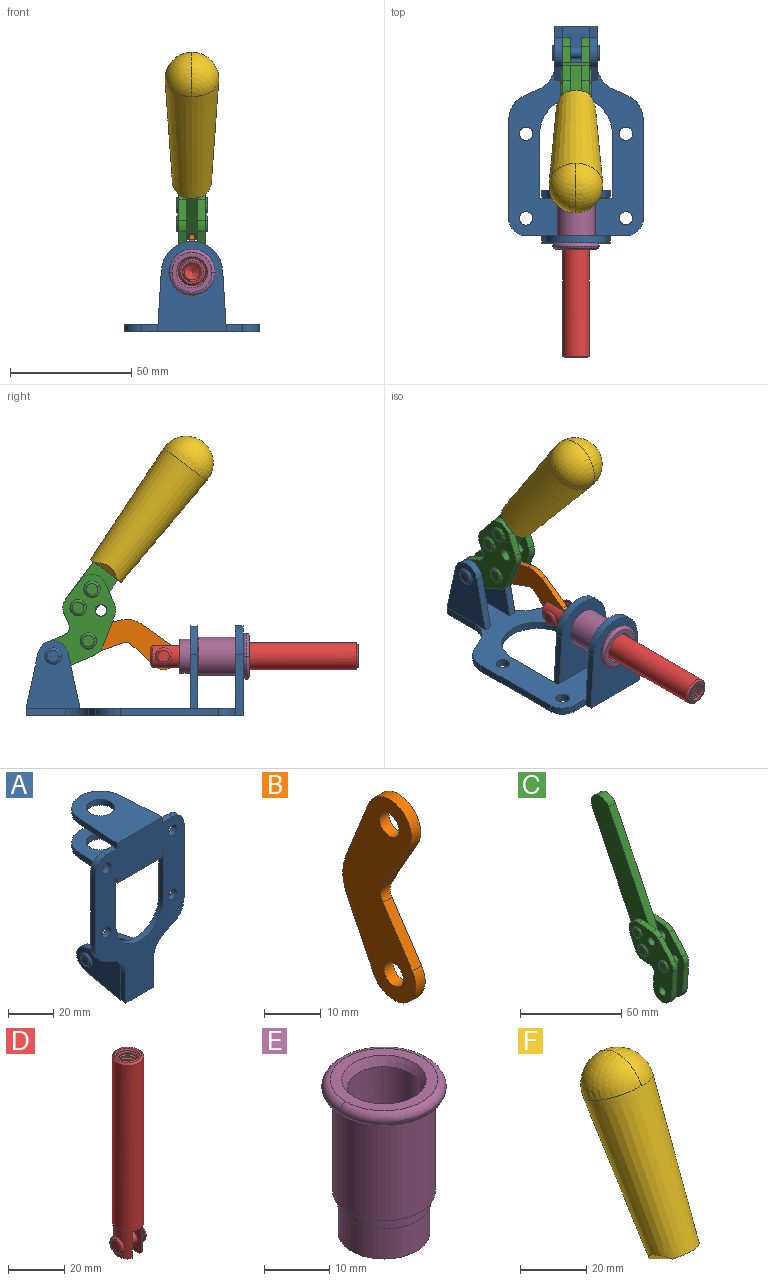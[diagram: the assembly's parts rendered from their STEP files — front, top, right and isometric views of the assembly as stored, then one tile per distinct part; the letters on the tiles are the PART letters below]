
ASSEMBLY  parts=6 mates=6
PART A: 55 faces, bbox 55.7x37.4x89.8 mm
  f0: torus R=2.41mm, axis (-1,0,0), area 15mm2, adj f11,f15,f25
  f1: torus R=2.41mm, axis (-1,0,0), area 15mm2, adj f10,f12,f22
  f2: cylinder r=2.78mm len=5.56mm, axis (0,-1,0), area 54.2mm2, adj f30,f54
  f3: cylinder r=14.99mm len=29.97mm, axis (0,-1,0), area 145.9mm2, adj f30,f49,f53,f54
  f4: cylinder r=2.78mm len=5.56mm, axis (0,-1,0), area 54.2mm2, adj f30,f54
  f5: cylinder r=2.78mm len=5.56mm, axis (0,-1,0), area 54.2mm2, adj f30,f54
  f6: cylinder r=2.78mm len=5.56mm, axis (0,-1,0), area 54.2mm2, adj f30,f54
  f7: cylinder r=6.35mm len=12.7mm, axis (0,0,1), area 123.6mm2, adj f27,f51
  f8: cylinder r=6.35mm len=12.7mm, axis (0,0,-1), area 124.7mm2, adj f21,f35
  f9: cylinder r=2.41mm len=11.18mm, axis (-1,0,0), area 169.4mm2, adj f16,f19
  f10: plane 4.83x4.83mm, normal (1,0,0), area 18.3mm2, adj f1,f12
  f11: plane 4.83x4.83mm, normal (-1,0,0), area 18.3mm2, adj f0,f15
  f12: torus R=2.41mm, axis (-1,0,0), area 15mm2, adj f1,f10,f22
  f13: cylinder r=6.35mm len=12.41mm, axis (1,0,0), area 53.4mm2, adj f18,f19,f22,f23
  f14: cylinder r=6.35mm len=12.41mm, axis (-1,0,0), area 53.4mm2, adj f16,f17,f24,f25
  f15: torus R=2.41mm, axis (-1,0,0), area 15mm2, adj f0,f11,f25
  f16: plane 27.86x22.35mm, normal (1,0,0), area 425.4mm2, adj f9,f14,f17,f24,f30
  f17: plane 22.86x4.97mm, normal (0,0.21,0.98), area 72.5mm2, adj f14,f16,f25,f30
  f18: plane 22.86x4.97mm, normal (0,0.21,0.98), area 72.5mm2, adj f13,f19,f22,f30
  f19: plane 27.86x22.35mm, normal (-1,0,0), area 425.4mm2, adj f9,f13,f18,f23,f30
  f20: cylinder r=12.7mm len=25.35mm, axis (0,0,-1), area 119.8mm2, adj f21,f34,f35,f36
  f21: plane 34.21x28.07mm, normal (0,0,-1), area 702.4mm2, adj f8,f20,f30,f34,f36
  f22: plane 27.96x22.45mm, normal (1,0,0), area 407.2mm2, adj f1,f12,f13,f18,f23,f30,f42,f43
  f23: plane 22.86x4.97mm, normal (0,0.21,-0.98), area 72.5mm2, adj f13,f19,f22,f44
  f24: plane 22.86x4.97mm, normal (0,0.21,-0.98), area 72.5mm2, adj f14,f16,f25,f44
  f25: plane 27.86x22.35mm, normal (-1,0,0), area 407.1mm2, adj f0,f14,f15,f17,f24,f30,f45,f46
  f26: plane 3.1x0.95mm, normal (0,0,-1), area 2.7mm2, adj f30,f49,f50,f54
  f27: plane 34.21x28.07mm, normal (0,0,1), area 702.4mm2, adj f7,f28,f30,f50,f52
  f28: cylinder r=12.7mm len=25.35mm, axis (0,0,1), area 118.8mm2, adj f27,f50,f51,f52
  f29: plane 3.1x0.95mm, normal (0,0,-1), area 2.7mm2, adj f30,f52,f53,f54
  f30: plane 86.54x55.63mm, normal (0,1,0), area 2362.9mm2, adj f2,f3,f4,f5,f6,f16,f17,f18
  f31: plane 40.56x3.1mm, normal (-1,0,0), area 125.7mm2, adj f30,f32,f48,f54
  f32: cylinder r=7.11mm len=7.11mm, axis (0,-1,0), area 34.6mm2, adj f30,f31,f33,f54
  f33: plane 6.67x3.1mm, normal (0,0,1), area 20.4mm2, adj f30,f32,f34,f54
  f34: plane 25.39x3.13mm, normal (-1,0.06,0), area 79.5mm2, adj f20,f21,f33,f35,f54
  f35: plane 37.31x28.45mm, normal (0,0,1), area 789.9mm2, adj f8,f20,f34,f36,f54
  f36: plane 25.39x3.13mm, normal (1,0.06,0), area 79.5mm2, adj f20,f21,f35,f37,f54
  f37: plane 6.67x3.1mm, normal (0,0,1), area 20.4mm2, adj f30,f36,f38,f54
  f38: cylinder r=7.11mm len=7.11mm, axis (0,-1,0), area 34.6mm2, adj f30,f37,f39,f54
  f39: plane 40.56x3.1mm, normal (1,0,0), area 125.7mm2, adj f30,f38,f40,f54
  f40: cylinder r=11.18mm len=10.16mm, axis (0,-1,0), area 39.5mm2, adj f30,f39,f41,f54
  f41: plane 6.09x3.1mm, normal (0.42,0,-0.91), area 20.8mm2, adj f30,f40,f42,f54
  f42: cylinder r=11.18mm len=9.41mm, axis (0,-1,0), area 37.2mm2, adj f22,f30,f41,f43,f54
  f43: plane 16.5x3.1mm, normal (1,0,0), area 51.1mm2, adj f22,f42,f44,f54
  f44: plane 17.37x3.1mm, normal (0,0,-1), area 53.8mm2, adj f23,f24,f30,f43,f45,f54
  f45: plane 16.5x3.1mm, normal (-1,0,0), area 51.1mm2, adj f25,f44,f46,f54
  f46: cylinder r=11.18mm len=9.41mm, axis (0,-1,0), area 37.2mm2, adj f25,f30,f45,f47,f54
  f47: plane 6.09x3.1mm, normal (-0.42,0,-0.91), area 20.8mm2, adj f30,f46,f48,f54
  f48: cylinder r=11.18mm len=10.16mm, axis (0,-1,0), area 39.5mm2, adj f30,f31,f47,f54
  f49: plane 26.54x3.1mm, normal (-1,0,0), area 82.3mm2, adj f3,f26,f30,f54
  f50: plane 25.39x3.1mm, normal (1,0.06,0), area 78.8mm2, adj f26,f27,f28,f51,f54
  f51: plane 37.31x28.45mm, normal (0,0,-1), area 789.9mm2, adj f7,f28,f50,f52,f54
  f52: plane 25.39x3.1mm, normal (-1,0.06,0), area 78.8mm2, adj f27,f28,f29,f51,f54
  f53: plane 26.54x3.1mm, normal (1,0,0), area 82.3mm2, adj f3,f29,f30,f54
  f54: plane 89.66x55.63mm, normal (0,-1,0), area 2678.5mm2, adj f2,f3,f4,f5,f6,f26,f29,f31
PART B: 12 faces, bbox 2.3x18.2x42.8 mm
  f0: cylinder r=2.4mm len=4.8mm, axis (1,0,0), area 34.9mm2, adj f4,f11
  f1: cylinder r=10.41mm len=8.47mm, axis (1,0,0), area 20.2mm2, adj f4,f9,f10,f11
  f2: cylinder r=3.05mm len=3.16mm, axis (1,0,0), area 7.7mm2, adj f4,f6,f7,f11
  f3: cylinder r=2.4mm len=4.8mm, axis (1,0,0), area 34.9mm2, adj f4,f11
  f4: plane 42.81x18.23mm, normal (-1,0,0), area 414.1mm2, adj f0,f1,f2,f3,f5,f6,f7,f8
  f5: cylinder r=5.54mm len=10.67mm, axis (1,0,0), area 41.8mm2, adj f4,f6,f10,f11
  f6: plane 11.66x6.53mm, normal (0,-0.87,-0.49), area 30.9mm2, adj f2,f4,f5,f11
  f7: plane 11.17x7.33mm, normal (0,-0.84,0.55), area 30.9mm2, adj f2,f4,f8,f11
  f8: cylinder r=5.54mm len=10.51mm, axis (1,0,0), area 41.8mm2, adj f4,f7,f9,f11
  f9: plane 13.67x6.67mm, normal (0,0.9,-0.44), area 35.1mm2, adj f1,f4,f8,f11
  f10: plane 14.1x5.7mm, normal (0,0.93,0.37), area 35.1mm2, adj f1,f4,f5,f11
  f11: plane 42.81x18.23mm, normal (1,0,0), area 414.1mm2, adj f0,f1,f2,f3,f5,f6,f7,f8
PART C: 59 faces, bbox 12.9x60.2x99.6 mm
  f0: torus R=2.39mm, axis (-1,0,0), area 14.9mm2, adj f20,f43,f51
  f1: torus R=2.39mm, axis (-1,0,0), area 14.9mm2, adj f19,f42,f51
  f2: torus R=2.39mm, axis (-1,0,0), area 14.9mm2, adj f18,f35,f51
  f3: torus R=2.39mm, axis (-1,0,0), area 14.9mm2, adj f14,f17,f23
  f4: torus R=2.39mm, axis (-1,0,0), area 14.9mm2, adj f13,f16,f23
  f5: torus R=2.39mm, axis (-1,0,0), area 14.9mm2, adj f12,f15,f23
  f6: cylinder r=2.39mm len=4.78mm, axis (1,0,0), area 46.5mm2, adj f48,f50,f51
  f7: cylinder r=2.39mm len=4.78mm, axis (1,0,0), area 46.5mm2, adj f50,f51
  f8: cylinder r=6.35mm len=12.68mm, axis (1,0,0), area 61.8mm2, adj f38,f39,f50,f51
  f9: cylinder r=2.39mm len=4.78mm, axis (-1,0,0), area 70.5mm2, adj f46,f50
  f10: cylinder r=2.39mm len=4.78mm, axis (-1,0,0), area 46.5mm2, adj f23,f45,f46
  f11: cylinder r=2.39mm len=4.78mm, axis (-1,0,0), area 46.5mm2, adj f23,f46
  f12: plane 4.78x4.78mm, normal (1,0,0), area 17.9mm2, adj f5,f15
  f13: plane 4.78x4.78mm, normal (1,0,0), area 17.9mm2, adj f4,f16
  f14: plane 4.78x4.78mm, normal (1,0,0), area 17.9mm2, adj f3,f17
  f15: torus R=2.39mm, axis (-1,0,0), area 14.9mm2, adj f5,f12,f23
  f16: torus R=2.39mm, axis (-1,0,0), area 14.9mm2, adj f4,f13,f23
  f17: torus R=2.39mm, axis (-1,0,0), area 14.9mm2, adj f3,f14,f23
  f18: plane 4.78x4.78mm, normal (-1,0,0), area 17.9mm2, adj f2,f35
  f19: plane 4.78x4.78mm, normal (-1,0,0), area 17.9mm2, adj f1,f42
  f20: plane 4.78x4.78mm, normal (-1,0,0), area 17.9mm2, adj f0,f43
  f21: plane 2.26x0.2mm, normal (1,0,0), area 0.2mm2, adj f31,f44
  f22: plane 2.26x0.2mm, normal (-1,0,0), area 0.2mm2, adj f41,f44
  f23: plane 39.37x30.77mm, normal (1,0,0), area 565.5mm2, adj f3,f4,f5,f10,f11,f15,f16,f17
  f24: cylinder r=6.1mm len=4.15mm, axis (-1,0,0), area 14.7mm2, adj f23,f25,f32,f46
  f25: plane 10.25x9.01mm, normal (0,-0.75,0.66), area 42.3mm2, adj f23,f24,f26,f46
  f26: cylinder r=6.35mm len=4.64mm, axis (-1,0,0), area 15.6mm2, adj f23,f25,f27,f46
  f27: plane 15.84x3.1mm, normal (0,-1,-0.07), area 49.2mm2, adj f23,f26,f28,f46
  f28: cylinder r=6.35mm len=12.68mm, axis (-1,0,0), area 61.8mm2, adj f23,f27,f29,f46
  f29: plane 8.11x3.1mm, normal (0,1,0.07), area 25.2mm2, adj f23,f28,f30,f46
  f30: cylinder r=3.05mm len=3.25mm, axis (-1,0,0), area 14.8mm2, adj f23,f29,f31,f46
  f31: plane 5.99x3.1mm, normal (0,0.07,-1), area 18.6mm2, adj f21,f23,f30,f44,f46
  f32: plane 9.5x3.1mm, normal (0,-0.07,1), area 29.5mm2, adj f23,f24,f33,f46,f47
  f33: cylinder r=6.1mm len=8.63mm, axis (-1,0,0), area 39.1mm2, adj f23,f32,f34,f47
  f34: plane 8.65x3.96mm, normal (0,0.91,-0.42), area 29.5mm2, adj f23,f33,f44,f47
  f35: torus R=2.39mm, axis (-1,0,0), area 14.9mm2, adj f2,f18,f51
  f36: plane 10.25x9.01mm, normal (0,-0.75,0.66), area 42.3mm2, adj f37,f49,f50,f51
  f37: cylinder r=6.35mm len=4.64mm, axis (1,0,0), area 15.6mm2, adj f36,f38,f50,f51
  f38: plane 15.84x3.1mm, normal (0,-1,-0.07), area 49.2mm2, adj f8,f37,f50,f51
  f39: plane 8.11x3.1mm, normal (0,1,0.07), area 25.2mm2, adj f8,f40,f50,f51
  f40: cylinder r=3.05mm len=3.25mm, axis (1,0,0), area 14.8mm2, adj f39,f41,f50,f51
  f41: plane 5.99x3.1mm, normal (0,0.07,-1), area 18.6mm2, adj f22,f40,f44,f50,f51
  f42: torus R=2.39mm, axis (-1,0,0), area 14.9mm2, adj f1,f19,f51
  f43: torus R=2.39mm, axis (-1,0,0), area 14.9mm2, adj f0,f20,f51
  f44: cylinder r=6.35mm len=12.12mm, axis (-1,0,0), area 128.9mm2, adj f21,f22,f23,f31,f34,f41,f46,f47
  f45: plane 2.65x1.35mm, normal (1,0,0), area 1mm2, adj f10,f55
  f46: plane 39.08x20.42mm, normal (-1,0,0), area 412.5mm2, adj f9,f10,f11,f24,f25,f26,f27,f28
  f47: plane 77.62x39.82mm, normal (1,0,0), area 850mm2, adj f32,f33,f34,f44,f53,f54,f55
  f48: plane 2.65x1.35mm, normal (-1,0,0), area 1mm2, adj f6,f55
  f49: cylinder r=6.1mm len=4.15mm, axis (1,0,0), area 14.7mm2, adj f36,f50,f51,f56
  f50: plane 39.08x20.42mm, normal (1,0,0), area 412.5mm2, adj f6,f7,f8,f9,f36,f37,f38,f39
  f51: plane 39.37x30.77mm, normal (-1,0,0), area 565.5mm2, adj f0,f1,f2,f6,f7,f8,f35,f36
  f52: plane 8.65x3.96mm, normal (0,0.91,-0.42), area 29.5mm2, adj f44,f51,f57,f58
  f53: plane 68.49x33.4mm, normal (0,0.9,-0.44), area 358.1mm2, adj f44,f47,f54,f58
  f54: cylinder r=6.35mm len=12.06mm, axis (1,0,0), area 93.7mm2, adj f47,f53,f55,f58
  f55: plane 68.49x33.4mm, normal (0,-0.9,0.44), area 358.1mm2, adj f44,f45,f46,f47,f48,f50,f54,f58
  f56: plane 9.5x3.1mm, normal (0,-0.07,1), area 29.5mm2, adj f49,f50,f51,f57,f58
  f57: cylinder r=6.1mm len=8.63mm, axis (1,0,0), area 39.1mm2, adj f51,f52,f56,f58
  f58: plane 77.62x39.82mm, normal (-1,0,0), area 850mm2, adj f44,f52,f53,f54,f55,f56,f57
PART D: 48 faces, bbox 12.6x11.1x86.1 mm
  f0: torus R=2.41mm, axis (-1,0,0), area 15mm2, adj f30,f32,f34
  f1: torus R=2.41mm, axis (-1,0,0), area 15mm2, adj f29,f31,f33
  f2: cylinder r=5.54mm len=72.39mm, axis (0,0,1), area 2518.5mm2, adj f3,f4,f42,f43
  f3: cone r=5.54mm half-angle=45deg, axis (0,0,1), area 7.6mm2, adj f2,f5,f41
  f4: cone r=5.54mm half-angle=45deg, axis (0,0,-1), area 34.9mm2, adj f2,f39
  f5: cylinder r=5.08mm len=11.48mm, axis (0,0,1), area 108.3mm2, adj f3,f7,f8,f41
  f6: cylinder r=2.41mm len=4.83mm, axis (-1,0,0), area 71.2mm2, adj f40,f41
  f7: cylinder r=2.41mm len=4.83mm, axis (-1,0,0), area 7.6mm2, adj f5,f34
  f8: cone r=5.08mm half-angle=45deg, axis (0,0,1), area 10.6mm2, adj f5,f37,f41
  f9: cone r=3.98mm half-angle=45deg, axis (0,0,1), area 17.6mm2, adj f27,f39,f45,f46,f47
  f10: cylinder r=2.41mm len=4.83mm, axis (-1,0,0), area 7.6mm2, adj f33,f38
  f11: cylinder r=3.2mm len=6.4mm, axis (0,0,1), area 78.4mm2, adj f12,f28,f44,f45,f47
  f12: cylinder r=3.2mm len=6.4mm, axis (0,0,1), area 10.5mm2, adj f11,f13,f45,f47
  f13: cylinder r=3.2mm len=6.4mm, axis (0,0,1), area 10.5mm2, adj f12,f14,f45,f47
  f14: cylinder r=3.2mm len=6.4mm, axis (0,0,1), area 10.5mm2, adj f13,f15,f45,f47
  f15: cylinder r=3.2mm len=6.4mm, axis (0,0,1), area 10.5mm2, adj f14,f16,f45,f47
  f16: cylinder r=3.2mm len=6.4mm, axis (0,0,1), area 10.5mm2, adj f15,f17,f45,f47
  f17: cylinder r=3.2mm len=6.4mm, axis (0,0,1), area 10.5mm2, adj f16,f18,f45,f47
  f18: cylinder r=3.2mm len=6.4mm, axis (0,0,1), area 10.5mm2, adj f17,f19,f45,f47
  f19: cylinder r=3.2mm len=6.4mm, axis (0,0,1), area 10.5mm2, adj f18,f20,f45,f47
  f20: cylinder r=3.2mm len=6.4mm, axis (0,0,1), area 10.5mm2, adj f19,f21,f45,f47
  f21: cylinder r=3.2mm len=6.4mm, axis (0,0,1), area 10.5mm2, adj f20,f22,f45,f47
  f22: cylinder r=3.2mm len=6.4mm, axis (0,0,1), area 10.5mm2, adj f21,f23,f45,f47
  f23: cylinder r=3.2mm len=6.4mm, axis (0,0,1), area 10.5mm2, adj f22,f24,f45,f47
  f24: cylinder r=3.2mm len=6.4mm, axis (0,0,1), area 10.5mm2, adj f23,f25,f45,f47
  f25: cylinder r=3.2mm len=6.4mm, axis (0,0,1), area 10.5mm2, adj f24,f26,f45,f47
  f26: cylinder r=3.2mm len=6.4mm, axis (0,0,1), area 10.5mm2, adj f25,f27,f45,f47
  f27: cylinder r=3.2mm len=6.4mm, axis (0,0,1), area 7.4mm2, adj f9,f26,f45,f47
  f28: cone r=3.2mm half-angle=60deg, axis (0,0,1), area 37.2mm2, adj f11
  f29: plane 4.83x4.83mm, normal (-1,0,0), area 18.3mm2, adj f1,f31
  f30: plane 4.83x4.83mm, normal (1,0,0), area 18.3mm2, adj f0,f32
  f31: torus R=2.41mm, axis (-1,0,0), area 15mm2, adj f1,f29,f33
  f32: torus R=2.41mm, axis (-1,0,0), area 15mm2, adj f0,f30,f34
  f33: plane 6.83x6.83mm, normal (1,0,0), area 18.3mm2, adj f1,f10,f31
  f34: plane 6.83x6.83mm, normal (-1,0,0), area 18.3mm2, adj f0,f7,f32
  f35: cone r=5.08mm half-angle=45deg, axis (0,0,1), area 10.6mm2, adj f36,f38,f40
  f36: plane 7.25x1.97mm, normal (0,0,-1), area 10mm2, adj f35,f40
  f37: plane 7.25x1.97mm, normal (0,0,-1), area 10mm2, adj f8,f41
  f38: cylinder r=5.08mm len=11.48mm, axis (0,0,1), area 108.3mm2, adj f10,f35,f40,f42
  f39: plane 9.55x9.55mm, normal (0,0,1), area 22mm2, adj f4,f9
  f40: plane 12.76x10.09mm, normal (1,0,0), area 95.7mm2, adj f6,f35,f36,f38,f42,f43
  f41: plane 12.76x10.09mm, normal (-1,0,0), area 95.7mm2, adj f3,f5,f6,f8,f37,f43
  f42: cone r=5.54mm half-angle=45deg, axis (0,0,1), area 7.6mm2, adj f2,f38,f40
  f43: plane 11.07x4.7mm, normal (0,0,-1), area 50.4mm2, adj f2,f40,f41
  f44: plane 0.89x0.62mm, normal (-1,0,0), area 0.3mm2, adj f11,f45,f46,f47
  f45: bspline ~24.8x7.63mm, area 266.6mm2, adj f9,f11,f12,f13,f14,f15,f16,f17
  f46: bspline ~24.87x7.63mm, area 73.6mm2, adj f9,f44,f45,f47
  f47: bspline ~24.98x7.63mm, area 272.5mm2, adj f9,f11,f12,f13,f14,f15,f16,f17
PART E: 15 faces, bbox 20.6x20.6x28.7 mm
  f0: torus R=8.26mm, axis (0,0,1), area 56.8mm2, adj f1,f10,f12
  f1: torus R=8.26mm, axis (0,0,1), area 56.8mm2, adj f0,f6,f13
  f2: cylinder r=5.59mm len=25.91mm, axis (0,0,1), area 909.6mm2, adj f3,f4
  f3: cone r=6.86mm half-angle=45deg, axis (0,0,-1), area 70.2mm2, adj f2,f14
  f4: cone r=6.47mm half-angle=30deg, axis (0,0,1), area 66.7mm2, adj f2,f13
  f5: cylinder r=7.04mm len=14.07mm, axis (0,0,1), area 252.6mm2, adj f11,f14
  f6: torus R=8.26mm, axis (0,0,1), area 56.8mm2, adj f1,f12,f13
  f7: cylinder r=7.16mm len=14.33mm, axis (0,0,1), area 91.5mm2, adj f9,f11
  f8: cylinder r=7.86mm len=18.42mm, axis (0,0,1), area 909.6mm2, adj f9,f10
  f9: plane 15.72x15.72mm, normal (0,0,-1), area 33mm2, adj f7,f8
  f10: plane 16.51x16.51mm, normal (0,0,-1), area 19.9mm2, adj f0,f8,f12
  f11: plane 14.33x14.33mm, normal (0,0,-1), area 5.7mm2, adj f5,f7
  f12: torus R=8.26mm, axis (0,0,1), area 56.8mm2, adj f0,f6,f10
  f13: plane 16.51x16.51mm, normal (0,0,1), area 82.7mm2, adj f1,f4,f6
  f14: plane 14.07x14.07mm, normal (0,0,-1), area 7.8mm2, adj f3,f5
PART F: 11 faces, bbox 22.3x42.6x64.5 mm
  f0: sphere r=11.13mm, area 411.4mm2, adj f1,f8
  f1: cone r=11.11mm half-angle=3.3deg, axis (0,0.44,0.9), area 3251.8mm2, adj f0,f7,f8,f9,f10
  f2: cylinder r=6.16mm len=11.7mm, axis (1,0,0), area 89.5mm2, adj f3,f4,f5,f6
  f3: plane 60.23x36.75mm, normal (-1,0,0), area 763.6mm2, adj f2,f4,f6,f10
  f4: plane 51.37x25.05mm, normal (0,0.9,-0.44), area 264.2mm2, adj f2,f3,f5,f10
  f5: plane 60.23x36.75mm, normal (1,0,0), area 763.6mm2, adj f2,f4,f6,f10
  f6: plane 51.37x25.05mm, normal (0,-0.9,0.44), area 264.2mm2, adj f2,f3,f5,f10
  f7: plane 9.95x5.95mm, normal (0.71,-0.31,-0.64), area 25.8mm2, adj f1,f10
  f8: sphere r=11.13mm, area 411.4mm2, adj f0,f1
  f9: plane 9.95x5.95mm, normal (-0.71,-0.31,-0.64), area 25.8mm2, adj f1,f10
  f10: plane 14.27x11.38mm, normal (0,-0.44,-0.9), area 106.7mm2, adj f1,f3,f4,f5,f6,f7,f9
PLACE A rot(axis=(1,0,0),90deg) t=(0,9.43,0)mm fixed
PLACE B rot(axis=(1,0,0),103.4deg) t=(0,16.56,4.25)mm
PLACE C rot(axis=(1,0,0),62.8deg) t=(0,1.72,17.42)mm
PLACE D rot(axis=(1,0,0),90deg) t=(0,11.28,0)mm
PLACE E rot(axis=(1,0,0),90deg) t=(0,9.43,0)mm
PLACE F rot(axis=(1,0,0),62.8deg) t=(-0.04,1.72,17.42)mm
MATE revolute B.f5 <-> D.f6  axis (1,0,0) through (0,-4.19,24.61)mm
MATE fastened E.f0 <-> A.f7  axis (0,1,0) through (0,-36.96,24.61)mm
MATE fastened C.f54 <-> F.f2  axis (-1,0,0) through (-2.35,-14.46,105.65)mm
MATE revolute C.f7 <-> A.f0  axis (1,0,0) through (0,41.52,24.61)mm
MATE slider D.f2 <-> A.f7  axis (0,-1,0) through (0,-47.5,24.61)mm
MATE revolute B.f3 <-> C.f4  axis (1,0,0) through (0,26.94,30.88)mm
